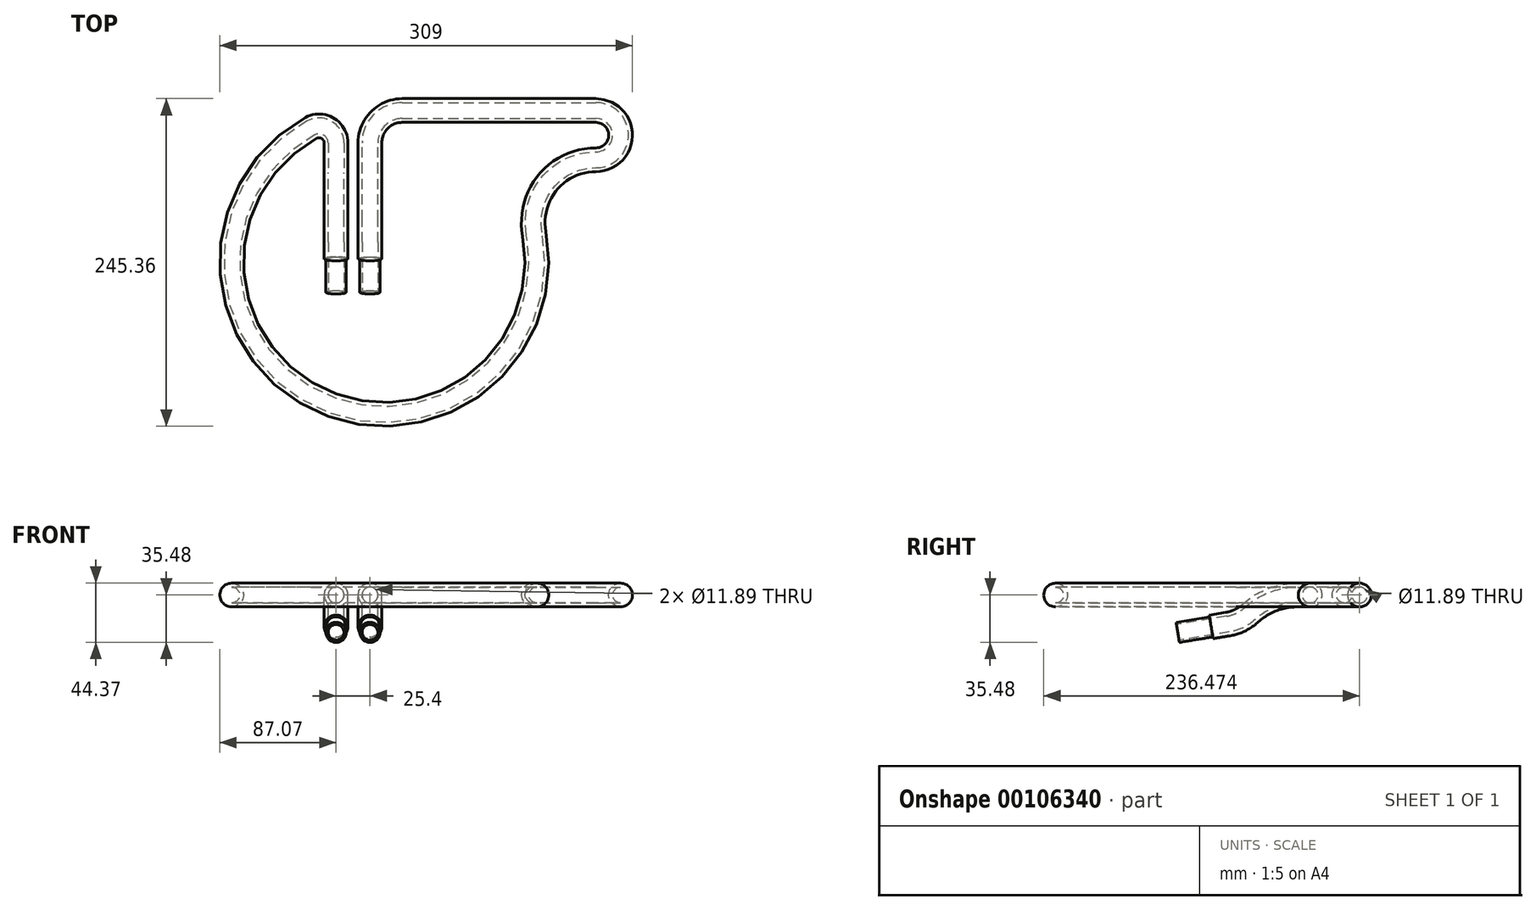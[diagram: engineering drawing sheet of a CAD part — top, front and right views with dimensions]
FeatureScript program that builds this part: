
annotation { "Feature Type Name" : "Feature", "Feature Type Description" : "" }
export const myFeature = defineFeature(function(context is Context, id is Id, definition is map)
    precondition{}
    {
        {
            var Q0;
            Q0=qCreatedBy(makeId("Top.planeOp"),FACE);
            var sketch = newSketch(context, id + "F0", { "sketchPlane" : qUnion([Q0])});
            skLineSegment(sketch, "E0", {"start": v(0, 0) * mm, "end": v(0, 12.7) * mm});
            skLineSegment(sketch, "E1", {"start": v(-25.4, 0) * mm, "end": v(0, 0) * mm});
            skArc(sketch, "E2", {"start": v(-25.4, 12.7) * mm, "mid": v(-31.63, 23.63) * mm, "end": v(-44.2, 23.84) * mm});
            skArc(sketch, "E3", {"start": v(0, 12.7) * mm, "mid": v(7.08, 29.8) * mm, "end": v(24.18, 36.88) * mm});
            skArc(sketch, "E4", {"start": v(-44.2, 23.84) * mm, "mid": v(-38.26, -179.68) * mm, "end": v(123.09, -55.49) * mm});
            skLineSegment(sketch, "E5", {"start": v(24.18, 36.88) * mm, "end": v(53.67, 36.88) * mm});
            skLineSegment(sketch, "E6", {"start": v(53.67, 36.88) * mm, "end": v(169.2, 36.88) * mm});
            skArc(sketch, "E7", {"start": v(123.09, -55.49) * mm, "mid": v(133.12, -16.93) * mm, "end": v(169.2, 0) * mm});
            skLineSegment(sketch, "E8", {"start": v(169.2, 0) * mm, "end": v(169.2, 0) * mm});
            skLineSegment(sketch, "E9", {"start": v(169.2, 36.88) * mm, "end": v(169.2, 0) * mm});
            skLineSegment(sketch, "E10", {"start": v(-25.4, 12.7) * mm, "end": v(-25.4, 0) * mm});
            skArc(sketch, "E11", {"start": v(169.2, 36.88) * mm, "mid": v(187.64, 18.44) * mm, "end": v(169.2, 0) * mm});
            skLineSegment(sketch, "E12", {"start": v(10.72, -76.4) * mm, "end": v(-103.58, -76.4) * mm});
            skSolve(sketch);
        }
        {
            var Q0;
            Q0=qCreatedBy(makeId("Front.planeOp"),FACE);
            var sketch = newSketch(context, id + "F1", { "sketchPlane" : qUnion([Q0])});
            skCircle(sketch, "E13", {"center": v(0, 0) * mm, "radius": 5.94 * mm});
            skCircle(sketch, "E14", {"center": v(0, 0) * mm, "radius": 8.9 * mm});
            skSolve(sketch);
        }
        {
            var Q0;
            Q0=makeQuery(id+"F1.imprint","IMPRINT",FACE,{"disambiguationData":[TD([[makeQuery(id+"F1.imprint","IMPRINT",EDGE,{"derivedFrom":sQuery(id+"F1.wireOp",EDGE,"E13")}),-1.0]])]});
            var Q1;
            Q1=sQuery(id+"F0.wireOp",EDGE,"E0");
            var Q2;
            Q2=sQuery(id+"F0.wireOp",EDGE,"E3");
            var Q3;
            Q3=sQuery(id+"F0.wireOp",EDGE,"E5");
            var Q4;
            Q4=sQuery(id+"F0.wireOp",EDGE,"E6");
            var Q5;
            Q5=sQuery(id+"F0.wireOp",EDGE,"E11");
            var Q6;
            Q6=sQuery(id+"F0.wireOp",EDGE,"E8");
            var Q7;
            Q7=sQuery(id+"F0.wireOp",EDGE,"E7");
            var Q8;
            Q8=sQuery(id+"F0.wireOp",EDGE,"E4");
            var Q9;
            Q9=sQuery(id+"F0.wireOp",EDGE,"E2");
            var Q10;
            Q10=sQuery(id+"F0.wireOp",EDGE,"E10");
            sweep(context, id + "F2", {"profiles" : qUnion([Q0]), "path" : qUnion([Q1, Q2, Q3, Q4, Q5, Q6, Q7, Q8, Q9, Q10])});
        }
        {
            var Q0;
            Q0=qCreatedBy(makeId("Right.planeOp"),FACE);
            var sketch = newSketch(context, id + "F3", { "sketchPlane" : qUnion([Q0])});
            skLineSegment(sketch, "E15", {"start": v(0, 0) * mm, "end": v(-9.55, 0) * mm});
            skArc(sketch, "E16", {"start": v(-9.55, 0) * mm, "mid": v(-28.53, -3.54) * mm, "end": v(-44.94, -13.7) * mm});
            skArc(sketch, "E17", {"start": v(-44.94, -13.7) * mm, "mid": v(-52.7, -18.95) * mm, "end": v(-61.63, -21.78) * mm});
            skLineSegment(sketch, "E18", {"start": v(-61.63, -21.78) * mm, "end": v(-99.22, -27.96) * mm});
            skSolve(sketch);
        }
        {
            var Q0;
            Q0=makeQuery(id+"F1.imprint","IMPRINT",FACE,{"disambiguationData":[TD([[makeQuery(id+"F1.imprint","IMPRINT",EDGE,{"derivedFrom":sQuery(id+"F1.wireOp",EDGE,"E13")}),-1.0]])]});
            var Q1;
            Q1=makeQuery(id+"F2.opSweep","CAP_FACE",FACE,{"disambiguationData":[OSD([sQuery(id+"F0.wireOp",VERTEX,"E10.end"),sQuery(id+"F1.wireOp",EDGE,"E13"),sQuery(id+"F1.wireOp",EDGE,"E14")])],"isStart":false});
            var Q2;
            Q2=sQuery(id+"F3.wireOp",EDGE,"E15");
            var Q3;
            Q3=sQuery(id+"F3.wireOp",EDGE,"E16");
            var Q4;
            Q4=sQuery(id+"F3.wireOp",EDGE,"E17");
            var Q5;
            Q5=sQuery(id+"F3.wireOp",EDGE,"E18");
            sweep(context, id + "F4", {"operationType" : NewBodyOperationType.ADD, "profiles" : qUnion([Q0, Q1]), "path" : qUnion([Q2, Q3, Q4, Q5])});
        }
        {
            var Q0;
            Q0=makeQuery(id+"F4.opSweep","CAP_FACE",FACE,{"disambiguationData":[OSD([sQuery(id+"F0.wireOp",VERTEX,"E10.end"),sQuery(id+"F1.wireOp",EDGE,"E13"),sQuery(id+"F1.wireOp",EDGE,"E14"),sQuery(id+"F3.wireOp",VERTEX,"E18.end")])],"isStart":false});
            var sketch = newSketch(context, id + "F5", { "sketchPlane" : qUnion([Q0])});
            skCircle(sketch, "E19", {"center": v(-25.4, -11.48) * mm, "radius": 7.62 * mm});
            skSolve(sketch);
        }
        {
            var Q0;
            Q0=makeQuery(id+"F4.opSweep","CAP_FACE",FACE,{"disambiguationData":[OSD([sQuery(id+"F1.wireOp",EDGE,"E13"),sQuery(id+"F1.wireOp",EDGE,"E14"),sQuery(id+"F3.wireOp",VERTEX,"E18.end")])],"isStart":false});
            var sketch = newSketch(context, id + "F6", { "sketchPlane" : qUnion([Q0])});
            skCircle(sketch, "E20", {"center": v(0, -11.48) * mm, "radius": 7.62 * mm});
            skSolve(sketch);
        }
        {
            var Q0;
            Q0=makeQuery(id+"F5.imprint","IMPRINT",FACE,{"disambiguationData":[TD([[makeQuery(id+"F5.imprint","IMPRINT",EDGE,{"derivedFrom":sQuery(id+"F5.wireOp",EDGE,"E19")}),-1.0]])]});
            extrude(context, id + "F7", {"entities" : qUnion([Q0]), "operationType" : NewBodyOperationType.REMOVE, "oppositeDirection" : true, "depth" : 25.4 * mm});
        }
        {
            var Q0;
            Q0=makeQuery(id+"F6.imprint","IMPRINT",FACE,{"disambiguationData":[TD([[makeQuery(id+"F6.imprint","IMPRINT",EDGE,{"derivedFrom":sQuery(id+"F6.wireOp",EDGE,"E20")}),-1.0]])]});
            extrude(context, id + "F8", {"entities" : qUnion([Q0]), "operationType" : NewBodyOperationType.REMOVE, "oppositeDirection" : true, "depth" : 25.4 * mm});
        }
    });
